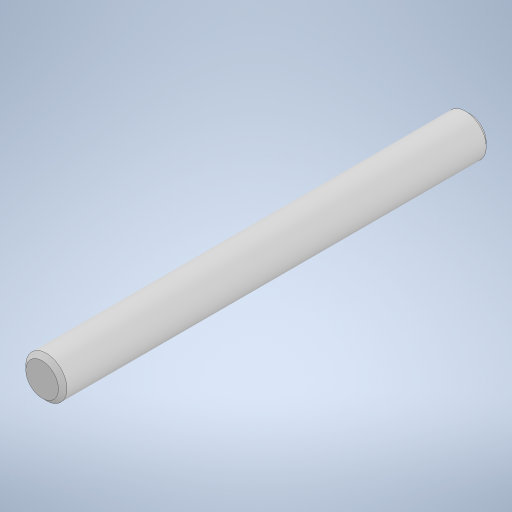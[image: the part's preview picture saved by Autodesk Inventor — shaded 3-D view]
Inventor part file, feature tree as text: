
AUTODESK INVENTOR PART (.ipt)
format: ipt  version: 2023 (Build 270158000, 158)  size: 231,424 bytes
history: native  units: in
note: dims shown in document units (in); Inventor stores cm internally (conversion verified against a paired STEP export)
features: extrude x1, chamfer x1, sketch x1
ambient origin geometry x8: Origin, YZ Plane, XZ Plane, XY Plane, X Axis, Y Axis, Z Axis, Center Point
bodies: Solid1 (feature_tree)
feature tree (3):
  extrude  "Extrusion1"  Depth=1.9685in TaperAngle=0.0deg
  chamfer  "Chamfer1"  Distance=0.0197in Angle=45.0deg
  sketch  "Sketch1"  dims[d0=0.189in d1=1.9685in d2=0.0in d3=0.0197in d4=0.0787in d5=45.0deg]
